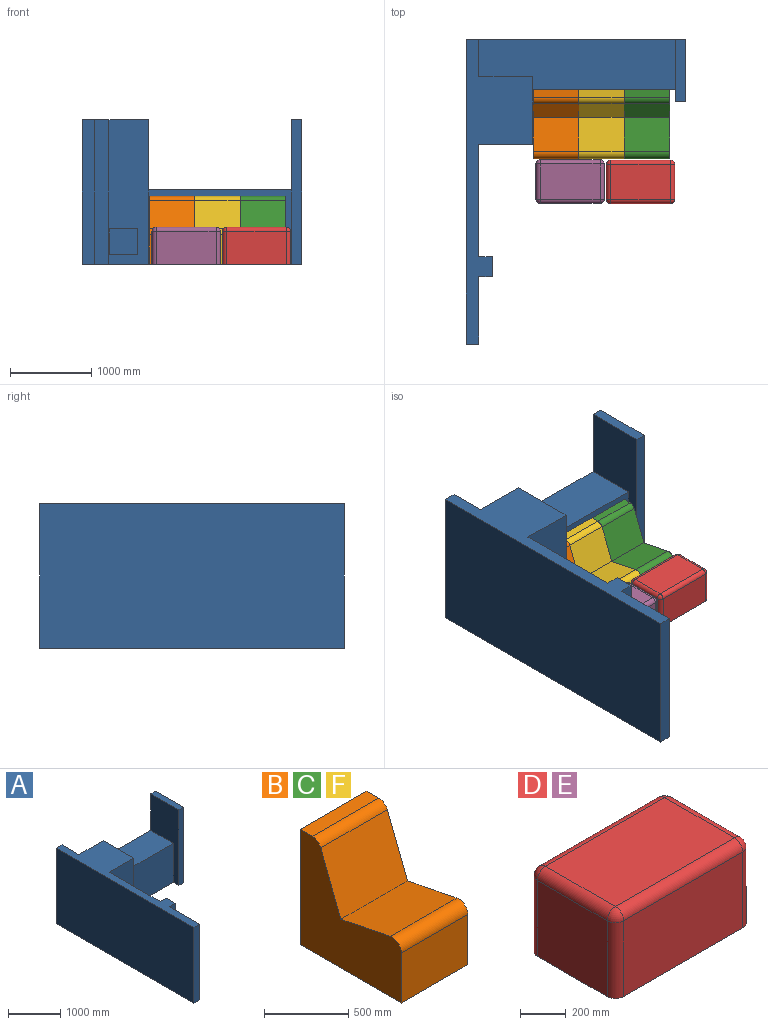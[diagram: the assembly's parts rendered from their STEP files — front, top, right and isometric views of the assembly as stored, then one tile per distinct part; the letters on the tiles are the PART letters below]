
ASSEMBLY  parts=6 mates=4
PART A: 26 faces, bbox 2692.4x3737.5x1778 mm
  f0: plane 346.64x76.2mm, normal (0,0,1), area 26414mm2, adj f1,f22,f23,f25
  f1: plane 1778x660.4mm, normal (0,-1,0), area 1066016.5mm2, adj f0,f3,f4,f5,f13,f21,f22,f23
  f2: plane 863.6x660.4mm, normal (0,1,0), area 570321.4mm2, adj f3,f4,f12,f19
  f3: plane 1778x825.5mm, normal (1,0,0), area 1328384.4mm2, adj f1,f2,f4,f5,f11,f12
  f4: plane 3737.55x812.8mm, normal (0,0,1), area 1154600.9mm2, adj f1,f2,f3,f7,f13,f14,f15,f16
  f5: plane 3737.55x2692.4mm, normal (0,0,-1), area 2542452.8mm2, adj f1,f3,f6,f7,f8,f9,f11,f13
  f6: plane 1778x762mm, normal (1,0,0), area 1354836mm2, adj f5,f7,f9,f10
  f7: plane 2692.4x1778mm, normal (0,1,0), area 2703220.4mm2, adj f4,f5,f6,f8,f10,f12,f14,f19
  f8: plane 1778x762mm, normal (-1,0,0), area 797417.8mm2, adj f5,f7,f9,f10,f11,f12
  f9: plane 1778x127mm, normal (0,-1,0), area 225806mm2, adj f5,f6,f8,f10
  f10: plane 762x127mm, normal (0,0,1), area 96774mm2, adj f6,f7,f8,f9
  f11: plane 1752.6x914.4mm, normal (0,-1,0), area 1602577.4mm2, adj f3,f5,f8,f12
  f12: plane 2413x609.6mm, normal (0,0,1), area 1370319.8mm2, adj f2,f3,f7,f8,f11,f19
  f13: plane 1778x1384.3mm, normal (1,0,0), area 2461285.4mm2, adj f1,f4,f5,f20
  f14: plane 3737.55x1778mm, normal (-1,0,0), area 6645357mm2, adj f4,f5,f7,f15
  f15: plane 1778x152.4mm, normal (0,-1,0), area 270967.2mm2, adj f4,f5,f14,f16
  f16: plane 1778x829.25mm, normal (1,0,0), area 1474399.6mm2, adj f4,f5,f15,f17
  f17: plane 1778x165.1mm, normal (0,-1,0), area 293547.8mm2, adj f4,f5,f16,f18
  f18: plane 1778x241.3mm, normal (1,0,0), area 429031.4mm2, adj f4,f5,f17,f20
  f19: plane 863.6x457.2mm, normal (1,0,0), area 394837.9mm2, adj f2,f4,f7,f12
  f20: plane 1778x165.1mm, normal (0,1,0), area 293547.8mm2, adj f4,f5,f13,f18
  f21: plane 346.64x304.8mm, normal (0,0,-1), area 105655.9mm2, adj f1,f22,f23,f24
  f22: plane 435.4x304.8mm, normal (1,0,0), area 123312.9mm2, adj f0,f1,f5,f21,f24,f25
  f23: plane 435.4x304.8mm, normal (-1,0,0), area 123312.9mm2, adj f0,f1,f5,f21,f24,f25
  f24: plane 435.4x346.64mm, normal (0,-1,0), area 150928.6mm2, adj f5,f21,f22,f23
  f25: plane 346.64x123.34mm, normal (0,1,0), area 42753.9mm2, adj f0,f5,f22,f23
PART B: 10 faces, bbox 558.8x850.9x838.2 mm
  f0: plane 558.8x416.86mm, normal (0,0.2,0.98), area 237552.2mm2, adj f1,f7,f8,f9
  f1: cylinder r=76.2mm len=558.8mm, axis (-1,0,0), area 75290.6mm2, adj f0,f2,f8,f9
  f2: plane 558.8x364.25mm, normal (0,-1,0), area 203543.4mm2, adj f1,f3,f8,f9
  f3: plane 850.9x558.8mm, normal (0,0,-1), area 475482.9mm2, adj f2,f4,f8,f9
  f4: plane 838.2x558.8mm, normal (0,1,0), area 468386.2mm2, adj f3,f5,f8,f9
  f5: plane 558.8x102.58mm, normal (0,0,1), area 57320.5mm2, adj f4,f6,f8,f9
  f6: cylinder r=76.2mm len=558.8mm, axis (-1,0,0), area 51048.5mm2, adj f5,f7,f8,f9
  f7: plane 558.8x434.09mm, normal (0,-0.93,0.36), area 260372.8mm2, adj f0,f6,f8,f9
  f8: plane 850.9x838.2mm, normal (1,0,0), area 446008mm2, adj f0,f1,f2,f3,f4,f5,f6,f7
  f9: plane 850.9x838.2mm, normal (-1,0,0), area 446008mm2, adj f0,f1,f2,f3,f4,f5,f6,f7
PART C: same geometry as B
PART D: 18 faces, bbox 838.2x533.4x457.2 mm
  f0: plane 431.8x406.4mm, normal (1,0,0), area 175483.5mm2, adj f5,f8,f14,f17
  f1: plane 736.6x406.4mm, normal (0,1,0), area 299354.2mm2, adj f5,f11,f15,f17
  f2: plane 431.8x406.4mm, normal (-1,0,0), area 175483.5mm2, adj f5,f6,f10,f11
  f3: plane 736.6x406.4mm, normal (0,-1,0), area 299354.2mm2, adj f5,f6,f8,f9
  f4: plane 736.6x431.8mm, normal (0,0,1), area 318063.9mm2, adj f9,f10,f14,f15
  f5: plane 838.2x533.4mm, normal (0,0,-1), area 444880.6mm2, adj f0,f1,f2,f3,f6,f8,f11,f17
  f6: cylinder r=50.8mm len=406.4mm, axis (0,0,1), area 32429.3mm2, adj f2,f3,f5,f7
  f7: sphere r=50.8mm, area 4053.7mm2, adj f6,f9,f10
  f8: cylinder r=50.8mm len=406.4mm, axis (0,0,-1), area 32429.3mm2, adj f0,f3,f5,f12
  f9: cylinder r=50.8mm len=736.6mm, axis (-1,0,0), area 58778.1mm2, adj f3,f4,f7,f12
  f10: cylinder r=50.8mm len=431.8mm, axis (0,1,0), area 34456.1mm2, adj f2,f4,f7,f13
  f11: cylinder r=50.8mm len=406.4mm, axis (0,0,-1), area 32429.3mm2, adj f1,f2,f5,f13
  f12: sphere r=50.8mm, area 4053.7mm2, adj f8,f9,f14
  f13: sphere r=50.8mm, area 4053.7mm2, adj f10,f11,f15
  f14: cylinder r=50.8mm len=431.8mm, axis (0,-1,0), area 34456.1mm2, adj f0,f4,f12,f16
  f15: cylinder r=50.8mm len=736.6mm, axis (1,0,0), area 58778.1mm2, adj f1,f4,f13,f16
  f16: sphere r=50.8mm, area 4053.7mm2, adj f14,f15,f17
  f17: cylinder r=50.8mm len=406.4mm, axis (0,0,1), area 32429.3mm2, adj f0,f1,f5,f16
PART E: same geometry as D
PART F: same geometry as B
PLACE A t=(-1752.6,0,0)mm
PLACE B t=(-1466.32,0,0)mm
PLACE C t=(-348.72,0,0)mm
PLACE D t=(-426.77,-1133.56,0)mm
PLACE E t=(-1291.28,-1130.33,0)mm
PLACE F t=(-907.52,0,0)mm
MATE planar A.f11 <-> B.f4  axis (0,-1,0) through (-876.3,0,457.2)mm
MATE planar D.f5 <-> C.f3  axis (0,0,-1) through (-426.77,-1133.56,0)mm
MATE planar E.f5 <-> C.f3  axis (0,0,-1) through (-1291.28,-1130.33,0)mm
MATE planar A.f5 <-> B.f3  axis (0,0,-1) through (-1589.85,-174.98,0)mm
